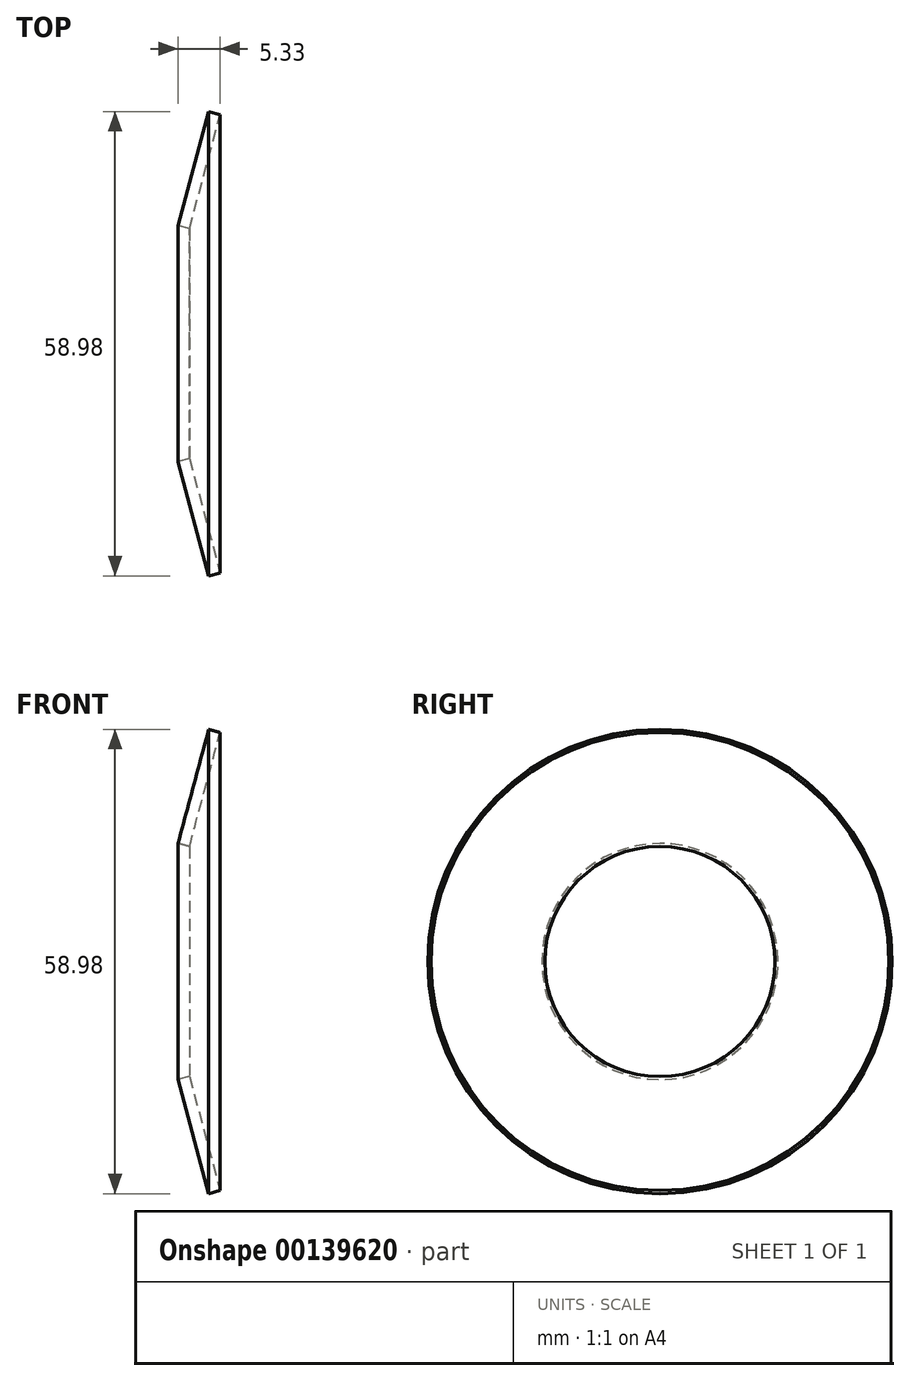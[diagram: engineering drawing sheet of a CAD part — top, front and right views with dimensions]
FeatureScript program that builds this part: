
annotation { "Feature Type Name" : "Feature", "Feature Type Description" : "" }
export const myFeature = defineFeature(function(context is Context, id is Id, definition is map)
    precondition{}
    {
        {
            var Q0;
            Q0=qCreatedBy(makeId("Front.planeOp"),FACE);
            var sketch = newSketch(context, id + "F0", { "sketchPlane" : qUnion([Q0])});
            skLineSegment(sketch, "E0", {"start": v(0, 15) * mm, "end": v(3.88, 29.49) * mm});
            skLineSegment(sketch, "E1", {"start": v(3.88, 29.49) * mm, "end": v(5.33, 29.1) * mm});
            skLineSegment(sketch, "E2", {"start": v(5.33, 29.1) * mm, "end": v(1.45, 14.61) * mm});
            skLineSegment(sketch, "E3", {"start": v(1.45, 14.61) * mm, "end": v(0, 15) * mm});
            skLineSegment(sketch, "E4", {"start": v(0, 0) * mm, "end": v(19.75, 0) * mm, "construction": true});
            skSolve(sketch);
        }
        {
            var Q0;
            Q0=makeQuery(id+"F0.imprint","IMPRINT",FACE,{"disambiguationData":[TD([[makeQuery(id+"F0.imprint","IMPRINT",EDGE,{"derivedFrom":sQuery(id+"F0.wireOp",EDGE,"E0")}),-1.0]])]});
            var Q1;
            Q1=sQuery(id+"F0.wireOp",EDGE,"E4");
            revolve(context, id + "F1", {"surfaceOperationType" : NewSurfaceOperationType.NEW, "entities" : qUnion([Q0]), "axis" : qUnion([Q1]), "revolveType" : RevolveType.ONE_DIRECTION, "angle" : 360 * degree});
        }
    });
